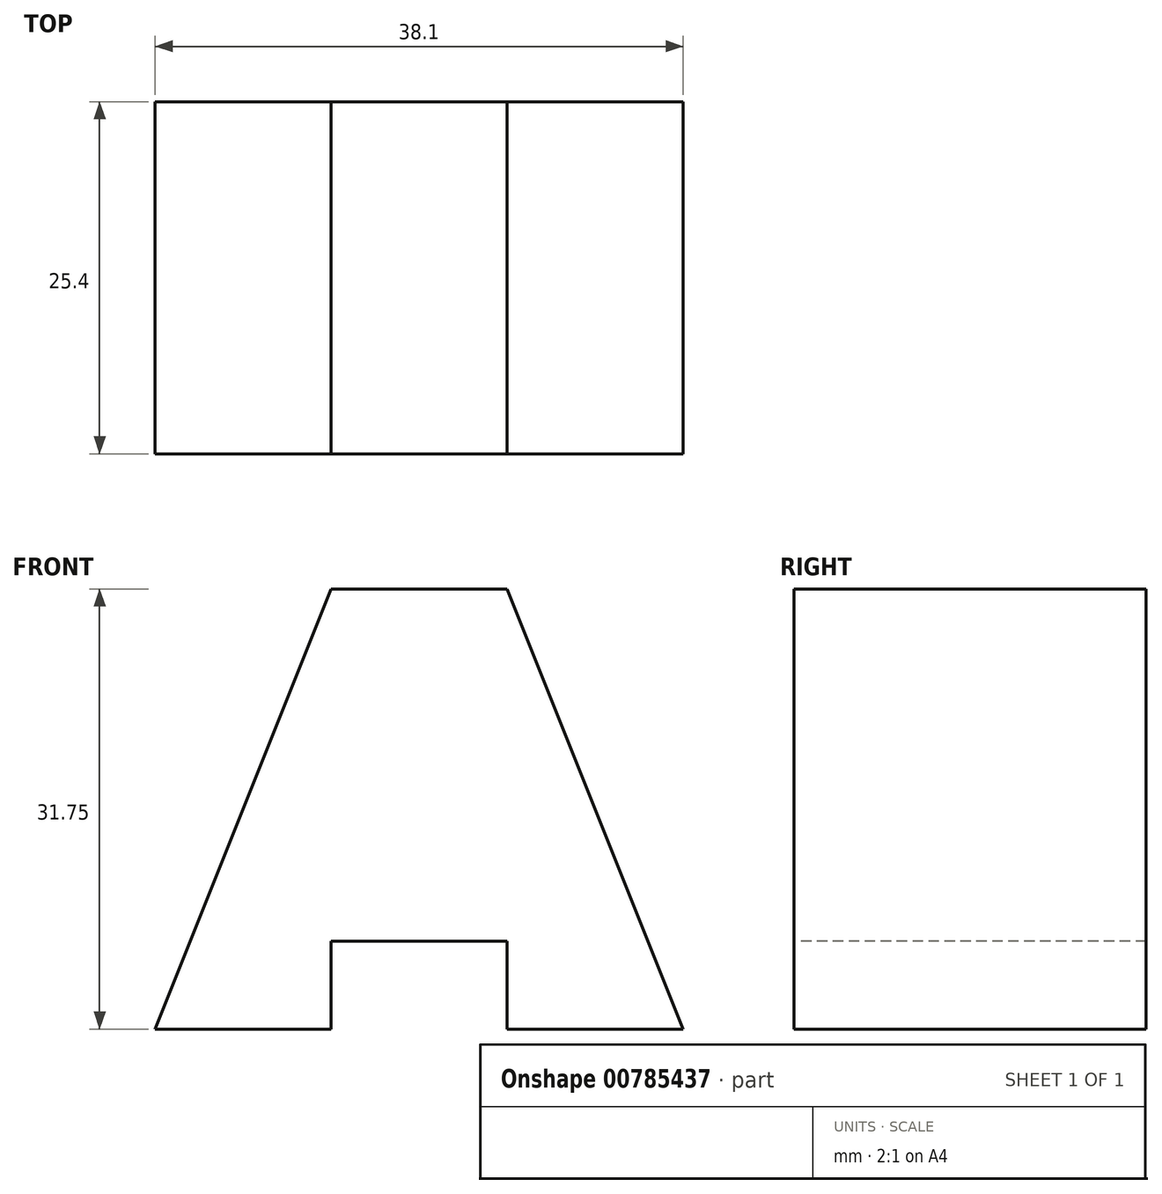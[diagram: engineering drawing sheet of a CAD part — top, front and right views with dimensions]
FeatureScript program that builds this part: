
annotation { "Feature Type Name" : "Feature", "Feature Type Description" : "" }
export const myFeature = defineFeature(function(context is Context, id is Id, definition is map)
    precondition{}
    {
        {
            var Q0;
            Q0=qCreatedBy(makeId("Front.planeOp"),FACE);
            var sketch = newSketch(context, id + "F0", { "sketchPlane" : qUnion([Q0])});
            skLineSegment(sketch, "E0", {"start": v(0, 0) * mm, "end": v(-12.7, 0) * mm});
            skLineSegment(sketch, "E1", {"start": v(-12.7, 0) * mm, "end": v(-12.7, 6.35) * mm});
            skLineSegment(sketch, "E2", {"start": v(-12.7, 6.35) * mm, "end": v(-25.4, 6.35) * mm});
            skLineSegment(sketch, "E3", {"start": v(-25.4, 6.35) * mm, "end": v(-25.4, 0) * mm});
            skLineSegment(sketch, "E4", {"start": v(-25.4, 0) * mm, "end": v(-38.1, 0) * mm});
            skLineSegment(sketch, "E5", {"start": v(-38.1, 0) * mm, "end": v(-25.4, 31.75) * mm});
            skLineSegment(sketch, "E6", {"start": v(-25.4, 31.75) * mm, "end": v(-12.7, 31.75) * mm});
            skLineSegment(sketch, "E7", {"start": v(-12.7, 31.75) * mm, "end": v(0, 0) * mm});
            skSolve(sketch);
        }
        {
            var Q0;
            Q0 = qSketchRegion(id + "F0", true);
            extrude(context, id + "F1", {"entities" : qUnion([Q0]), "oppositeDirection" : true, "depth" : 25.4 * mm, "offsetDistance" : 25.4 * mm});
        }
    });
